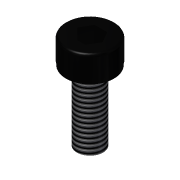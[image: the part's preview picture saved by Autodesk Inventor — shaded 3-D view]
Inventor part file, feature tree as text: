
AUTODESK INVENTOR PART (.ipt)
format: ipt  version: 2014 (Build 180170000, 170)  size: 119,296 bytes
history: native  units: mm
features: extrude x4, sketch x4, fillet x1, thread x1, reference x1
ambient origin geometry x8: Origin, YZ Plane, XZ Plane, XY Plane, X Axis, Y Axis, Z Axis, Center Point
bodies: Solid1 (feature_tree)
feature tree (11):
  extrude  "Extrusion1"  Depth=8.0mm TaperAngle=0.0deg
  extrude  "Extrusion2"  Depth=3.0mm TaperAngle=0.0deg
  fillet  "Fillet1"  Radius=0.3mm
  extrude  "Extrusion3"  Depth=0.5mm TaperAngle=0.0deg
  extrude  "Extrusion4"  Depth=2.0mm TaperAngle=0.0deg
  thread  "Thread1"  [1 undecoded]
  sketch  "Sketch1"  dims[d0=3.0mm d1=8.0mm d2=0.0mm]
  reference  "Reference1"
  sketch  "Sketch2"  dims[d3=5.6mm d4=3.0mm d5=0.0mm d6=0.3mm]
  sketch  "Sketch3"  dims[d7=5.5mm d8=0.5mm d9=0.0mm]
  sketch  "Sketch4"  dims[d10=2.5mm d11=2.0mm d12=0.0mm d13=10.0mm d14=0.0mm]
note: 1 required parameter value undecoded (feature->parameter linkage not recoverable at this tier; creation-order binding heuristic only, values carry confidence <= 0.55)
